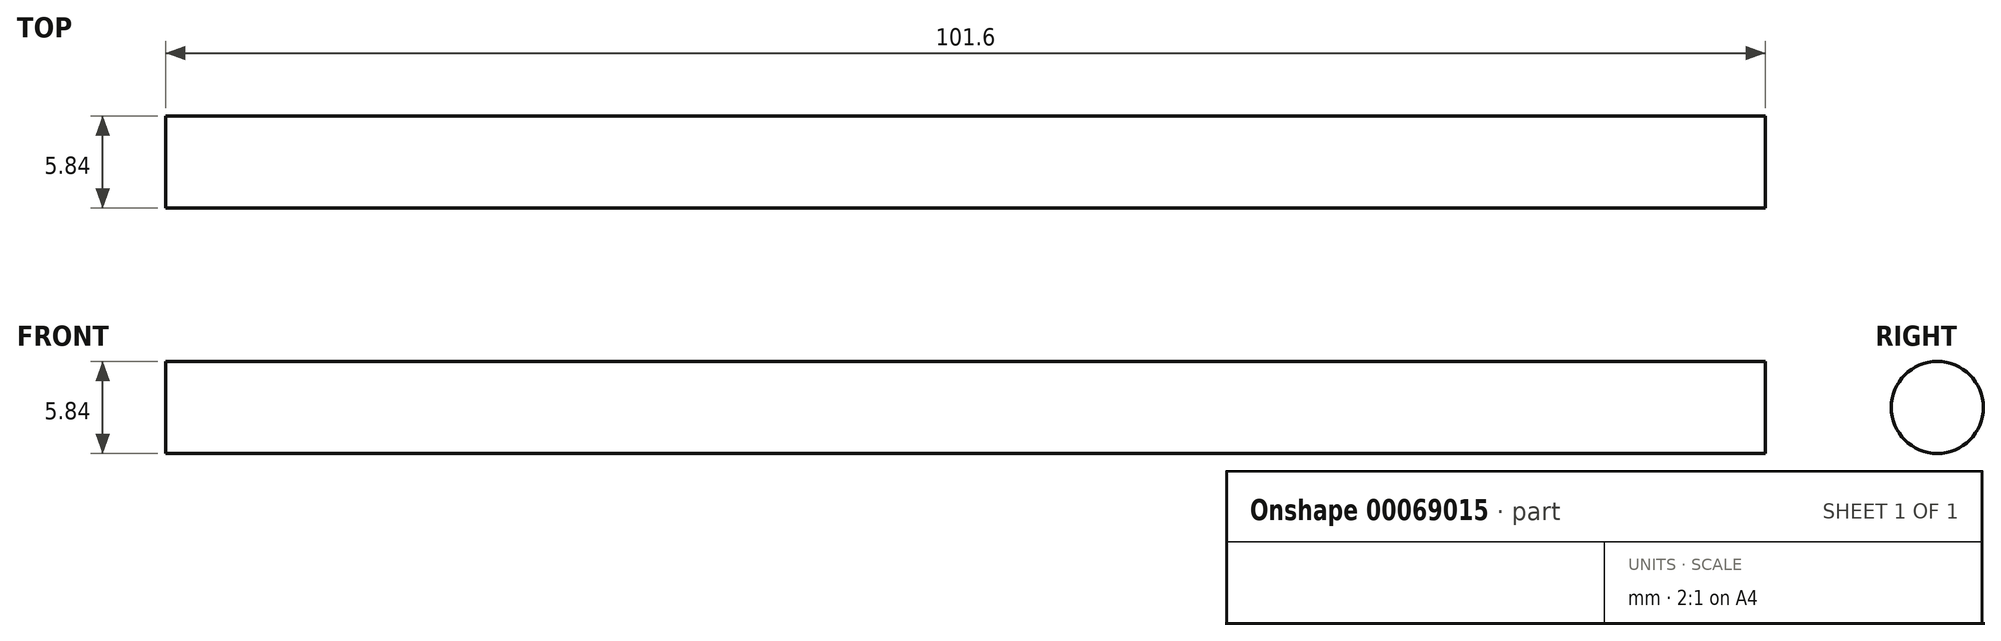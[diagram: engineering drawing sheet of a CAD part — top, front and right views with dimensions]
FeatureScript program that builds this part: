
annotation { "Feature Type Name" : "Feature", "Feature Type Description" : "" }
export const myFeature = defineFeature(function(context is Context, id is Id, definition is map)
    precondition{}
    {
        {
            var Q0;
            Q0=qCreatedBy(makeId("Right.planeOp"),FACE);
            var sketch = newSketch(context, id + "F0", { "sketchPlane" : qUnion([Q0])});
            skCircle(sketch, "E0", {"center": v(0, 0) * mm, "radius": 2.92 * mm});
            skSolve(sketch);
        }
        {
            var Q0;
            Q0 = qSketchRegion(id + "F0", true);
            extrude(context, id + "F1", {"entities" : qUnion([Q0]), "depth" : 101.6 * mm});
        }
    });
